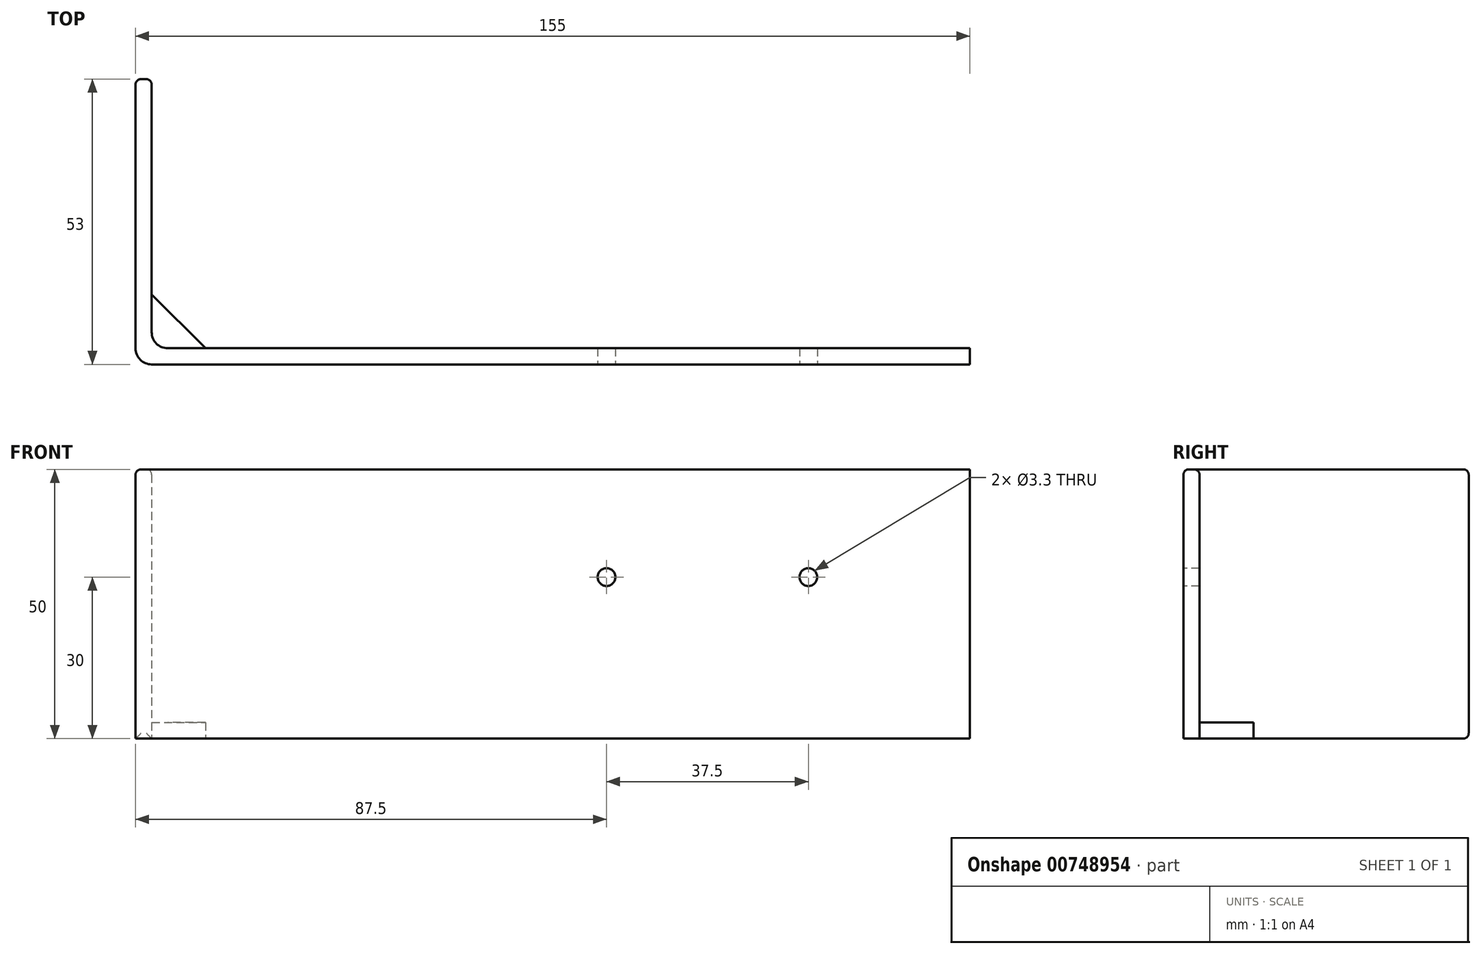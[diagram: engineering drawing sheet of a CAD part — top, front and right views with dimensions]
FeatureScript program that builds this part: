
annotation { "Feature Type Name" : "Feature", "Feature Type Description" : "" }
export const myFeature = defineFeature(function(context is Context, id is Id, definition is map)
    precondition{}
    {
        {
            var Q0;
            Q0=qCreatedBy(makeId("Top.planeOp"),FACE);
            var sketch = newSketch(context, id + "F0", { "sketchPlane" : qUnion([Q0])});
            skLineSegment(sketch, "E0.bottom", {"start": v(0, 0) * mm, "end": v(-155, 0) * mm});
            skLineSegment(sketch, "E0.top", {"start": v(0, 3) * mm, "end": v(-152, 3) * mm});
            skLineSegment(sketch, "E0.left", {"start": v(0, 0) * mm, "end": v(0, 3) * mm});
            skLineSegment(sketch, "E0.right", {"start": v(-155, 0) * mm, "end": v(-155, 3) * mm});
            skLineSegment(sketch, "E1.top", {"start": v(-155, 53) * mm, "end": v(-152, 53) * mm});
            skLineSegment(sketch, "E1.left", {"start": v(-155, 3) * mm, "end": v(-155, 53) * mm});
            skLineSegment(sketch, "E1.right", {"start": v(-152, 3) * mm, "end": v(-152, 3) * mm});
            skLineSegment(sketch, "E2", {"start": v(-152, 3) * mm, "end": v(-152, 53) * mm});
            skPoint(sketch, "E3", {"position": v(-152, 13) * mm});
            skPoint(sketch, "E4", {"position": v(-142, 3) * mm});
            skLineSegment(sketch, "E5", {"start": v(-152, 13) * mm, "end": v(-142, 3) * mm});
            skPoint(sketch, "E6", {"position": v(-67.5, 3) * mm});
            skPoint(sketch, "E7", {"position": v(-30, 3) * mm});
            skSolve(sketch);
        }
        {
            var Q0;
            Q0=makeQuery(id+"F0.imprint","IMPRINT",FACE,{"disambiguationData":[TD([[makeQuery(id+"F0.imprint","IMPRINT",EDGE,{"derivedFrom":sQuery(id+"F0.wireOp",EDGE,"E0.bottom")}),-1.0]])]});
            extrude(context, id + "F1", {"entities" : qUnion([Q0]), "depth" : 50 * mm, "offsetDistance" : 25 * mm});
        }
        {
            var Q0;
            {var subQ3=sQuery(id+"F0.wireOp",EDGE,"E5");Q0=makeQuery(id+"F0.imprint","IMPRINT",FACE,{"disambiguationData":[TD([[makeQuery(id+"F0.imprint","IMPRINT",EDGE,{"derivedFrom":subQ3}),-1.0]])]});}
            extrude(context, id + "F2", {"entities" : qUnion([Q0]), "operationType" : NewBodyOperationType.ADD, "depth" : 3 * mm, "offsetDistance" : 25 * mm});
        }
        {
            var Q0;
            Q0=makeQuery(id+"F1.opExtrude","SWEPT_EDGE",EDGE,{"disambiguationData":[OSD([sQuery(id+"F0.wireOp",EDGE,"E0.top"),sQuery(id+"F0.wireOp",EDGE,"E2")])]});
            fillet(context, id + "F3", {"entities" : qUnion([Q0]), "radius" : 3 * mm, "tangentPropagation" : true, "allowEdgeOverflow" : false});
        }
        {
            var Q0;
            Q0=makeQuery(id+"F1.opExtrude","SWEPT_EDGE",EDGE,{"disambiguationData":[OSD([sQuery(id+"F0.wireOp",EDGE,"E0.bottom"),sQuery(id+"F0.wireOp",EDGE,"E0.right")])]});
            fillet(context, id + "F4", {"entities" : qUnion([Q0]), "radius" : 3 * mm, "tangentPropagation" : true, "allowEdgeOverflow" : false});
        }
        {
            var Q0;
            Q0=qCreatedBy(makeId("Front.planeOp"),FACE);
            var sketch = newSketch(context, id + "F5", { "sketchPlane" : qUnion([Q0])});
            skPoint(sketch, "E8", {"position": v(-67.5, 30) * mm});
            skPoint(sketch, "E9", {"position": v(-30, 30) * mm});
            skSolve(sketch);
        }
        {
            var Q0;
            Q0=sQuery(id+"F5.wireOp",VERTEX,"E9");
            var Q1;
            Q1=sQuery(id+"F5.wireOp",VERTEX,"E8");
            var Q2;
            Q2=makeQuery(id+"F1.opExtrude","SWEPT_BODY",BODY,{"disambiguationData":[OSD([sQuery(id+"F0.wireOp",EDGE,"E0.bottom"),sQuery(id+"F0.wireOp",EDGE,"E0.top"),sQuery(id+"F0.wireOp",EDGE,"E0.left"),sQuery(id+"F0.wireOp",EDGE,"E0.right"),sQuery(id+"F0.wireOp",EDGE,"E1.top"),sQuery(id+"F0.wireOp",EDGE,"E1.left"),sQuery(id+"F0.wireOp",EDGE,"E2")])]});
            hole(context, id + "F6", {"style" : HoleStyle.SIMPLE, "endStyle" : HoleEndStyle.THROUGH, "standardTappedOrClearance" : lookupTablePath({ "standard" : "ISO", "fit" : "Normal", "size" : "M3", "type" : "Clearance" }), "standardBlindInLast" : lookupTablePath({ "fit" : "Standard", "standard" : "ISO", "size" : "M3", "type" : "Clearance" }), "holeDiameter" : 3.3 * mm, "majorDiameter" : 5 * mm, "isTappedThrough" : true, "tappedDepth" : 48.5 * mm, "tapClearance" : 3, "locations" : qUnion([Q0, Q1]), "scope" : qUnion([Q2])});
        }
        {
            var Q0;
            Q0=makeQuery(id+"F1.opExtrude","CAP_EDGE",EDGE,{"disambiguationData":[OSD([sQuery(id+"F0.wireOp",EDGE,"E0.bottom")])],"isStart":false});
            var Q1;
            Q1=makeQuery(id+"F1.opExtrude","CAP_EDGE",EDGE,{"disambiguationData":[OSD([sQuery(id+"F0.wireOp",EDGE,"E0.top")])],"isStart":false});
            var Q2;
            Q2=makeQuery(id+"F1.opExtrude","CAP_EDGE",EDGE,{"disambiguationData":[OSD([sQuery(id+"F0.wireOp",EDGE,"E0.right"),sQuery(id+"F0.wireOp",EDGE,"E1.left")])],"isStart":false});
            var Q3;
            Q3=makeQuery(id+"F1.opExtrude","CAP_EDGE",EDGE,{"disambiguationData":[OSD([sQuery(id+"F0.wireOp",EDGE,"E2")])],"isStart":false});
            var Q4;
            {var subQ0=sQuery(id+"F0.wireOp",EDGE,"E2");var subQ1=sQuery(id+"F0.wireOp",EDGE,"E0.top");Q4=makeQuery(id+"F3.opFillet","BLEND_EDGE",EDGE,{"blendedFrom":[makeQuery(id+"F1.opExtrude","SWEPT_EDGE",EDGE,{"disambiguationData":[OSD([subQ1,subQ0])]}),makeQuery(id+"F1.opExtrude","CAP_FACE",FACE,{"disambiguationData":[OSD([sQuery(id+"F0.wireOp",EDGE,"E0.bottom"),subQ1,sQuery(id+"F0.wireOp",EDGE,"E0.left"),sQuery(id+"F0.wireOp",EDGE,"E0.right"),sQuery(id+"F0.wireOp",EDGE,"E1.top"),sQuery(id+"F0.wireOp",EDGE,"E1.left"),subQ0])],"isStart":false})],"blendedInto":[makeQuery(id+"F1.opExtrude","CAP_FACE",FACE,{"disambiguationData":[OSD([sQuery(id+"F0.wireOp",EDGE,"E0.bottom"),subQ1,sQuery(id+"F0.wireOp",EDGE,"E0.left"),sQuery(id+"F0.wireOp",EDGE,"E0.right"),sQuery(id+"F0.wireOp",EDGE,"E1.top"),sQuery(id+"F0.wireOp",EDGE,"E1.left"),subQ0])],"isStart":false})]});}
            var Q5;
            {var subQ0=sQuery(id+"F0.wireOp",EDGE,"E0.right");var subQ1=sQuery(id+"F0.wireOp",EDGE,"E0.bottom");Q5=makeQuery(id+"F4.opFillet","BLEND_EDGE",EDGE,{"blendedFrom":[makeQuery(id+"F1.opExtrude","SWEPT_EDGE",EDGE,{"disambiguationData":[OSD([subQ1,subQ0])]}),makeQuery(id+"F1.opExtrude","CAP_FACE",FACE,{"disambiguationData":[OSD([subQ1,sQuery(id+"F0.wireOp",EDGE,"E0.top"),sQuery(id+"F0.wireOp",EDGE,"E0.left"),subQ0,sQuery(id+"F0.wireOp",EDGE,"E1.top"),sQuery(id+"F0.wireOp",EDGE,"E1.left"),sQuery(id+"F0.wireOp",EDGE,"E2")])],"isStart":false})],"blendedInto":[makeQuery(id+"F1.opExtrude","CAP_FACE",FACE,{"disambiguationData":[OSD([subQ1,sQuery(id+"F0.wireOp",EDGE,"E0.top"),sQuery(id+"F0.wireOp",EDGE,"E0.left"),subQ0,sQuery(id+"F0.wireOp",EDGE,"E1.top"),sQuery(id+"F0.wireOp",EDGE,"E1.left"),sQuery(id+"F0.wireOp",EDGE,"E2")])],"isStart":false})]});}
            fillet(context, id + "F7", {"entities" : qUnion([Q0, Q1, Q2, Q3, Q4, Q5]), "radius" : 1 * mm, "tangentPropagation" : true, "allowEdgeOverflow" : false});
        }
        {
            var Q0;
            Q0=makeQuery(id+"F1.opExtrude","SWEPT_EDGE",EDGE,{"disambiguationData":[OSD([sQuery(id+"F0.wireOp",EDGE,"E1.top"),sQuery(id+"F0.wireOp",EDGE,"E2")])]});
            var Q1;
            Q1=makeQuery(id+"F1.opExtrude","SWEPT_EDGE",EDGE,{"disambiguationData":[OSD([sQuery(id+"F0.wireOp",EDGE,"E1.top"),sQuery(id+"F0.wireOp",EDGE,"E1.left")])]});
            var Q2;
            Q2=makeQuery(id+"F1.opExtrude","SWEPT_FACE",FACE,{"disambiguationData":[OSD([sQuery(id+"F0.wireOp",EDGE,"E1.top")])]});
            fillet(context, id + "F8", {"entities" : qUnion([Q0, Q1, Q2]), "radius" : 1 * mm, "tangentPropagation" : true, "allowEdgeOverflow" : false});
        }
    });
